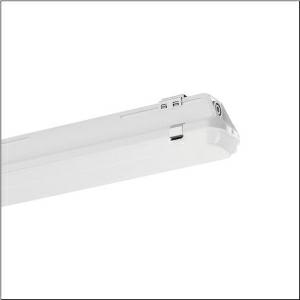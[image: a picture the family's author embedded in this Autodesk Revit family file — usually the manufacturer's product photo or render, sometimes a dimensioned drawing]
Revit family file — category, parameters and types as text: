
# Revit family: monsun_r__21_51fb207p460b005_f6e2
name_source: partatom
category: Lighting Fixtures
units: mm (PartAtom-declared; Revit-internal decimal feet)

## family parameters
Cut with Voids When Loaded = No
Host = Face
Light Source = No
Part Type = Normal
Room Calculation Point = No
Round Connector Dimension = Use Diameter
Shared = No

## types (1)
- Monsun® 21 (1 x LED, 5400 lm, 38 W, 4000K)
    Apparent Load = 38 VA
    CIE Flux Codes = 45 75 93 94 100
    Color Rendering = 80
    Color Temperature = 4000K
    Default Elevation = 1800 mm
    Description = Monsun® 21, damp-proof luminaire, chain hanger, primary optical cover: enclosure, of PC, light emission: direct distribution, primary light characteristic: symmetric, installation type: suspended mounting, surface-mounted, horizontal mounting, vertical mounting, LED, rated luminous flux: 5.400lm, luminous efficacy: 142lm/W, light colour: 840, colour temperature: 4000K, control gear: ECG, with terminal, 3-pole, max. 2.5mm², through-wiring: 5x 2.5mm², mains connection: 220..240V, AC, 50/60Hz, rated input power: 38W, housing, of glass-fibre reinforced polyester, uncoated, bright grey, length: 1.590mm, width: 90mm, height: 88mm, clip for enclosure, of stainless steel (V2A), ceiling mounting element, of stainless steel (V2A), chain hanger, of stainless steel (V2A), protection rating (complete): IP66, insulation class (complete): insulation class I (protective earthing), certification: CE, ENEC, VDE, UKCA, protection symbol: D, impact resistance: IK08, permissible operating ambient temperature: -25..+35°C, standard: EN 50419, EN 60598-2-1, corresponds to IFS (International Featured Standards) requirements for safety and quality in the food industry, for indoor or canopied outdoor use, no direct snow, no direct sun, no direct rain, packaging unit: 1 piece
    Height = 89 mm
    Lamp = 1 x LED
    Lamp Light Flux = 5400 lm
    Lamp Power = 38 W
    Lamp count = 1
    Length = 1590 mm
    Luminous efficacy = 142 lm/W
    Manufacturer = Siteco
    ModVariant = No
    Model = 51FB207P460B005
    Mounting Place = Ceiling
    Mounting Type = Pendant
    Number of Poles = 1
    OnlyDefault = Yes
    Power Factor = 1
    Product Name = Monsun® 21
    Product group = damp-proof luminaire | ceiling pendant
    ProductGroupID = 908
    Protection Class = Protection class I
    Protection Degree = IP 66
    RLX_Detail_Level = 1
    RlxData = <blob elided: 88173 chars, md5=d9715c4a>
    Socket = socket
    Standby Power = 0 W
    System Light Flux = 5400 lm
    System Power = 38 W
    Type Comments = Product without accessories
    Type Image = l_1006717.jpg
    URL = http://relux.com
    VarID = ---
    Voltage = 0 V
    Weight = 0.00 kg
    Width = 90 mm

## geometry (parser evidence)
native form markers: Blend x4, Sweep x15
no freeform markers — native parametric forms only
